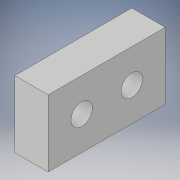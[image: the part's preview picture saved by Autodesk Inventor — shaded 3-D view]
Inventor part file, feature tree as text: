
AUTODESK INVENTOR PART (.ipt)
format: ipt  version: 2017 (Build 210142000, 142)  size: 112,640 bytes
history: native  units: in
note: dims shown in document units (in); Inventor stores cm internally (conversion verified against a paired STEP export)
features: sketch x3, hole x2, extrude x1
ambient origin geometry x8: Origin, YZ Plane, XZ Plane, XY Plane, X Axis, Y Axis, Z Axis, Center Point
bodies: Solid1 (feature_tree)
feature tree (6):
  extrude  "Extrusion1"  Depth=0.5in
  hole  "Hole1"  [1 undecoded]
  hole  "Hole2"  [1 undecoded]
  sketch  "Sketch1"  dims[d0=0.25in d1=0.5in]
  sketch  "Sketch2"  dims[d2=0.875in d3=0.0in d4=0.125in]
  sketch  "Sketch3"  dims[d5=0.125in d6=0.13in d7=0.155in d8=0.375in d9=0.25in d10=0.5635in d11=0.175in d12=0.8108in d14=0.375in d15=0.16in d16=0.125in d17=0.375in d18=0.25in d19=0.5635in d20=1.0in d21=0.8108in]
note: 2 required parameter values undecoded (feature->parameter linkage not recoverable at this tier; creation-order binding heuristic only, values carry confidence <= 0.55)
